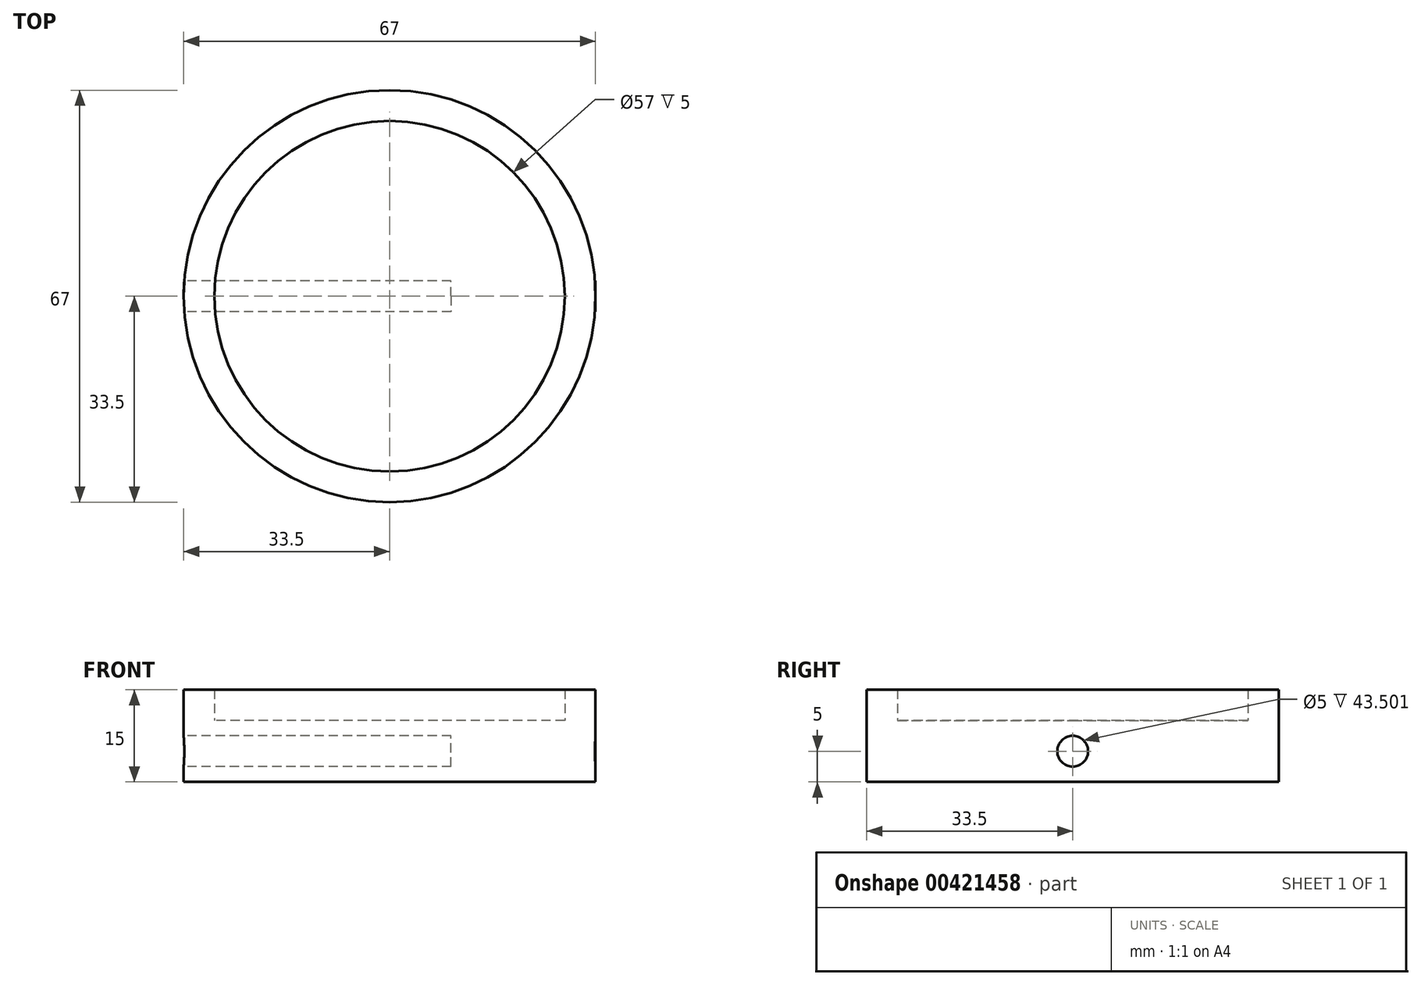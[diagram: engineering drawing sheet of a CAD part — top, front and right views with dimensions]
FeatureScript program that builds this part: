
annotation { "Feature Type Name" : "Feature", "Feature Type Description" : "" }
export const myFeature = defineFeature(function(context is Context, id is Id, definition is map)
    precondition{}
    {
        {
            var Q0;
            Q0=qCreatedBy(makeId("Top.planeOp"),FACE);
            var sketch = newSketch(context, id + "F0", { "sketchPlane" : qUnion([Q0])});
            skCircle(sketch, "E0", {"center": v(0, 0) * mm, "radius": 28.5 * mm});
            skCircle(sketch, "E1", {"center": v(0, 0) * mm, "radius": 33.5 * mm});
            skSolve(sketch);
        }
        {
            var Q0;
            Q0 = qSketchRegion(id + "F0", true);
            extrude(context, id + "F1", {"entities" : qUnion([Q0]), "depth" : 15 * mm});
        }
        {
            var Q0;
            Q0=makeQuery(id+"F0.imprint","IMPRINT",FACE,{"disambiguationData":[TD([[makeQuery(id+"F0.imprint","IMPRINT",EDGE,{"derivedFrom":sQuery(id+"F0.wireOp",EDGE,"E0")}),1.0]])]});
            extrude(context, id + "F2", {"entities" : qUnion([Q0]), "operationType" : NewBodyOperationType.ADD, "depth" : 10 * mm});
        }
        {
            var Q0;
            Q0=qCreatedBy(makeId("Right.planeOp"),FACE);
            var sketch = newSketch(context, id + "F3", { "sketchPlane" : qUnion([Q0])});
            skLineSegment(sketch, "E2", {"start": v(0, 0) * mm, "end": v(0, 5) * mm});
            skCircle(sketch, "E3", {"center": v(0, 5) * mm, "radius": 2.5 * mm});
            skSolve(sketch);
        }
        {
            var Q0;
            Q0 = qSketchRegion(id + "F3", true);
            extrude(context, id + "F4", {"entities" : qUnion([Q0]), "operationType" : NewBodyOperationType.REMOVE, "endBound" : BoundingType.SYMMETRIC, "depth" : 70 * mm});
        }
        {
            var Q0;
            Q0=makeQuery(id+"F3.imprint","IMPRINT",FACE,{"disambiguationData":[TD([[makeQuery(id+"F3.imprint","IMPRINT",EDGE,{"derivedFrom":sQuery(id+"F3.wireOp",EDGE,"E3")}),1.0]])]});
            extrude(context, id + "F5", {"entities" : qUnion([Q0]), "operationType" : NewBodyOperationType.ADD, "depth" : 33.5 * mm});
        }
        {
            var Q0;
            Q0=makeQuery(id+"F3.imprint","IMPRINT",FACE,{"disambiguationData":[TD([[makeQuery(id+"F3.imprint","IMPRINT",EDGE,{"derivedFrom":sQuery(id+"F3.wireOp",EDGE,"E3")}),1.0]])]});
            extrude(context, id + "F6", {"entities" : qUnion([Q0]), "operationType" : NewBodyOperationType.REMOVE, "depth" : 10 * mm});
        }
    });
